# Revit family: Drain_Floor-Jay R.Smith-Round_Type-2335_Series
name_source: partatom
category: Plumbing Fixtures
units: mm (PartAtom-declared; Revit-internal decimal feet)

## family parameters
Always vertical = No
Cut with Voids When Loaded = No
OmniClass Number = 23.70.50.21.24
OmniClass Title = Waste Water Drains
Part Type = Normal
Room Calculation Point = No
Round Connector Dimension = Use Diameter
Shared = Yes
Work Plane-Based = Yes

## types (10) — shared parameters
Adjustable Extensions 4 1/2(115) to 6"(150) -E = No
Assembly Code = D2030300
CW Connection = No
D - Dome Grate = No
Default Elevation = 0"
Description = Medium Duty Floor Drains with 12" Adjustable Round Tops
Diameter = 15 1/4"
FBS - Flat Bottom Strainer = No
Finish = Cast_Iron-Jay R.Smith-Duco_Coated
G - Galvanized Cast Iron = No
Grate Material = Cast_Iron-Jay R.Smith-Duco_Coated
H - Hinged Grate = No
HW Connection = No
Installation Type = Floor Mounted
L - Speedi-Set Service Weight 02(50), 03(80) & 04"(100) sizes only (Fig. 2330 only) = No
LXH - Speedi-Set Extra HeavY 02(50), 03(80) & 04"(100) sizes only (Fig. 2330 only = No
M - Ductile Iron Grate = No
Manufacturer = Jay R. Smith
Material = Cast_Iron-Jay R.Smith-Duco_Coated
NB - Nickel Bronze Top = No
NO-HUB Adaptor = No
PB - Polished Bronze Top = No
Product Documentation Link = https://www.jrsmith.com
Product Page URL = https://www.jrsmith.com
Quad Close Trap Seal = No
S - Square Top = No
Strainer Inner Diameter = 11 1/2"
Strainer Outer Diameter = 12"
Trap Primer Connection -P050   1/2" (13) & -P075 3/4" (19) = No
U - Vandal Proof Grate = No
URL = http://www.jrsmith.com
Vent Connection = No
Waste Connection = Yes
zero-valued in all types: CWFU, HWFU, WFU

## per-type parameters (varying)
| type | A | B | C | Connection Type | D | E | F | Outlet Diameter | Outlet Radius | T-Threaded Outlet |
| 2335C02 | 2" | 6 7/8" | 4 3/4" | 2"Caulk Outlet Connection | 6" | 7 1/4" | 8 5/8" | 2" | 1" | No |
| 2335C03 | 3" | 6 3/8" | 4 3/4" | 3" Caulk Outlet Connection | 6" | 7 1/2" | 8 3/4" | 3" | 1 1/2" | No |
| 2335C04 | 4" | 5 7/8" | 4 3/4" | 4" Caulk Outlet Connection | 6" | 7 3/4" | 8 3/4" | 4" | 2" | No |
| 2335C05 | 5" | 5" | 6 1/4" | 5" Caulk Outlet Connection | 6 5/8" | 7 3/4" | 8 1/2" | 5" | 2 1/2" | No |
| 2335C06 | 6" | 4 1/2" | 6 1/4" | 6" Caulk Outlet Connection | 6 7/8" | 7 3/4" | 8 1/2" | 6" | 3" | No |
| 2335Y02 | 2" | 6 7/8" | 4 3/4" | 2" Threaded Outlet Connection | 6" | 7 1/4" | 8 5/8" | 2" | 1" | Yes |
| 2335Y03 | 3" | 6 3/8" | 4 3/4" | 3" Threaded Outlet Connection | 6" | 7 1/2" | 8 3/4" | 3" | 1 1/2" | Yes |
| 2335Y04 | 4" | 5 7/8" | 4 3/4" | 4" Threaded Outlet Connection | 6" | 7 3/4" | 8 3/4" | 4" | 2" | Yes |
| 2335Y05 | 5" | 5" | 6 1/4" | 5" Threaded Outlet Connection | 6 5/8" | 7 3/4" | 8 1/2" | 5" | 2 1/2" | Yes |
| 2335Y06 | 6" | 4 1/2" | 6 1/4" | 6" Threaded Outlet Connection | 6 7/8" | 7 3/4" | 8 1/2" | 6" | 3" | Yes |

note: column(s) folded — value = type name in every type: Model

## geometry (parser evidence)
native form markers: Sweep x2
no freeform markers — native parametric forms only
